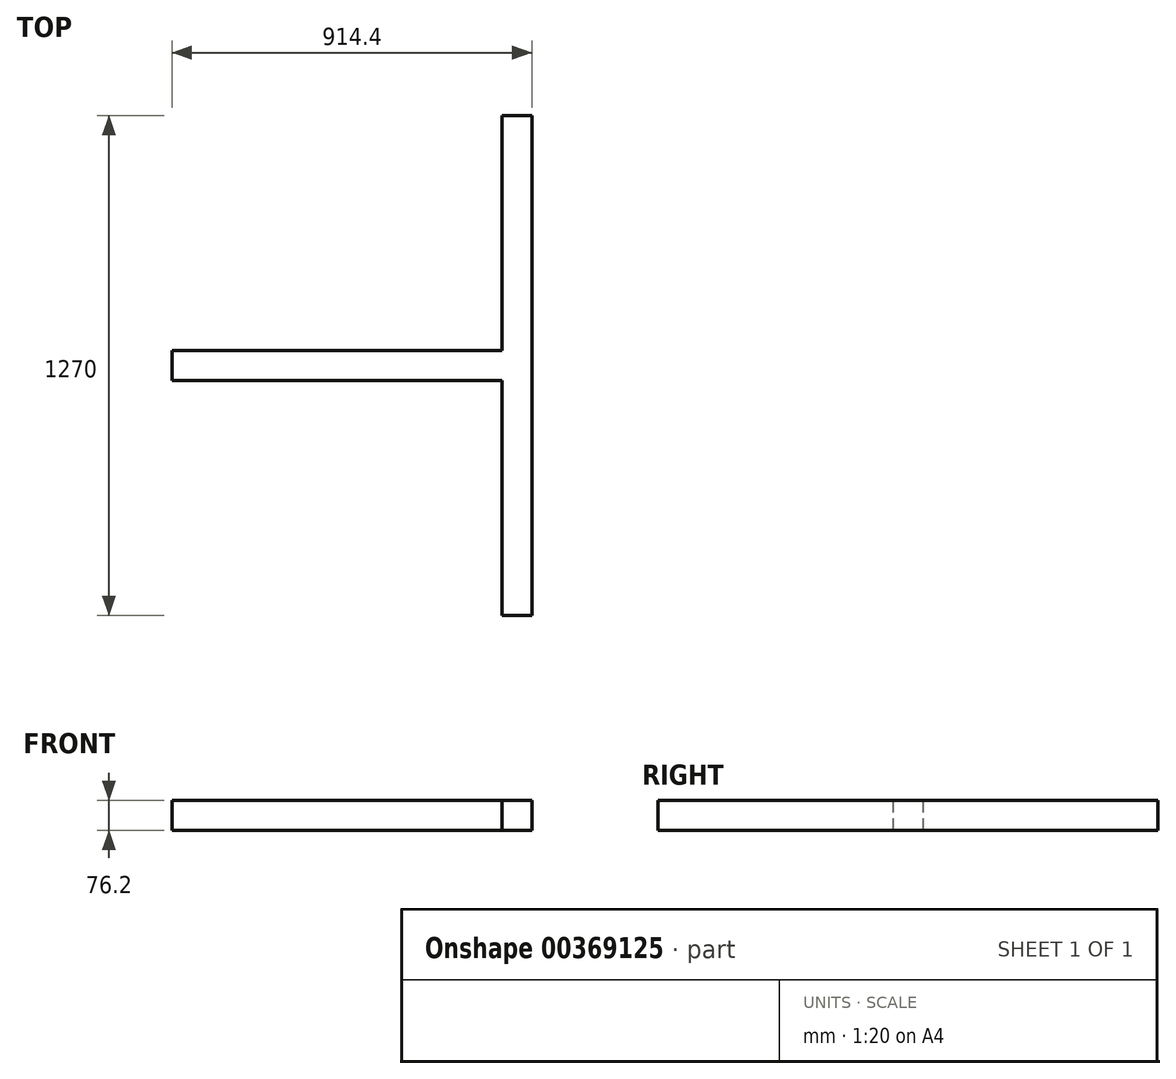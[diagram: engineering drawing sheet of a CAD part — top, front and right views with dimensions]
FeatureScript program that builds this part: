
annotation { "Feature Type Name" : "Feature", "Feature Type Description" : "" }
export const myFeature = defineFeature(function(context is Context, id is Id, definition is map)
    precondition{}
    {
        {
            var Q0;
            Q0=qCreatedBy(makeId("Top.planeOp"),FACE);
            var sketch = newSketch(context, id + "F0", { "sketchPlane" : qUnion([Q0])});
            skLineSegment(sketch, "E0.bottom", {"start": v(-419.1, -38.1) * mm, "end": v(419.1, -38.1) * mm});
            skLineSegment(sketch, "E0.top", {"start": v(-419.1, 38.1) * mm, "end": v(419.1, 38.1) * mm});
            skLineSegment(sketch, "E0.left", {"start": v(-419.1, -38.1) * mm, "end": v(-419.1, 38.1) * mm});
            skLineSegment(sketch, "E0.right", {"start": v(419.1, -38.1) * mm, "end": v(419.1, 38.1) * mm});
            skPoint(sketch, "E0.middle", {"position": v(0, 0) * mm});
            skLineSegment(sketch, "E1.bottom", {"start": v(-419.1, -38.1) * mm, "end": v(-342.9, -38.1) * mm});
            skLineSegment(sketch, "E1.top", {"start": v(-419.1, -1816.1) * mm, "end": v(-342.9, -1816.1) * mm});
            skLineSegment(sketch, "E1.left", {"start": v(-419.1, -38.1) * mm, "end": v(-419.1, -1816.1) * mm});
            skLineSegment(sketch, "E1.right", {"start": v(-342.9, -38.1) * mm, "end": v(-342.9, -1816.1) * mm});
            skLineSegment(sketch, "E2", {"start": v(419.1, 38.1) * mm, "end": v(419.1, 0) * mm});
            skLineSegment(sketch, "E3.bottom", {"start": v(495.3, 635) * mm, "end": v(419.1, 635) * mm});
            skLineSegment(sketch, "E3.top", {"start": v(495.3, -635) * mm, "end": v(419.1, -635) * mm});
            skLineSegment(sketch, "E3.left", {"start": v(495.3, 635) * mm, "end": v(495.3, -635) * mm});
            skPoint(sketch, "E3.middle", {"position": v(419.1, 0) * mm});
            skLineSegment(sketch, "E4", {"start": v(419.1, 635) * mm, "end": v(419.1, -635) * mm});
            skPoint(sketch, "E5.start.orphan", {"position": v(342.9, -635) * mm});
            skPoint(sketch, "E6.start.orphan", {"position": v(342.9, 635) * mm});
            skSolve(sketch);
        }
        {
            var Q0;
            {var subQ2=sQuery(id+"F0.wireOp",EDGE,"E3.bottom");Q0=makeQuery(id+"F0.imprint","IMPRINT",FACE,{"disambiguationData":[TD([[makeQuery(id+"F0.imprint","IMPRINT",EDGE,{"derivedFrom":subQ2}),1.0]])]});}
            var Q1;
            {var subQ2=sQuery(id+"F0.wireOp",EDGE,"E0.bottom");Q1=makeQuery(id+"F0.imprint","IMPRINT",FACE,{"disambiguationData":[TD([[makeQuery(id+"F0.imprint","IMPRINT",EDGE,{"derivedFrom":subQ2}),1.0]])]});}
            var Q2;
            Q2=makeQuery(id+"F0.imprint","IMPRINT",FACE,{"disambiguationData":[TD([[makeQuery(id+"F0.imprint","IMPRINT",EDGE,{"derivedFrom":sQuery(id+"F0.wireOp",EDGE,"E1.bottom")}),-1.0]])]});
            extrude(context, id + "F1", {"entities" : qUnion([Q0, Q1, Q2]), "depth" : 76.2 * mm});
        }
    });
